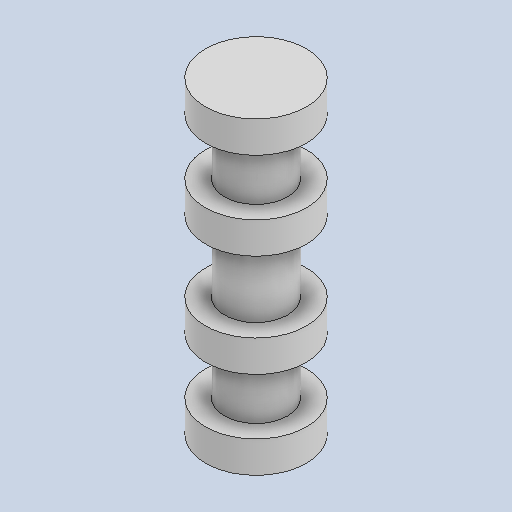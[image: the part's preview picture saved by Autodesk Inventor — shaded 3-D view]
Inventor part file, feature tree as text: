
AUTODESK INVENTOR PART (.ipt)
format: ipt  version: 2023 (Build 270158000, 158)  size: 275,968 bytes
history: native  units: in
note: dims shown in document units (in); Inventor stores cm internally (conversion verified against a paired STEP export)
features: revolve x1
ambient origin geometry x8: Origin, YZ Plane, XZ Plane, XY Plane, X Axis, Y Axis, Z Axis, Center Point
bodies: Solid1 (feature_tree)
feature tree (1):
  revolve  "Revolution1"  [1 undecoded]
note: 1 required parameter value undecoded (feature->parameter linkage not recoverable at this tier; creation-order binding heuristic only, values carry confidence <= 0.55)
